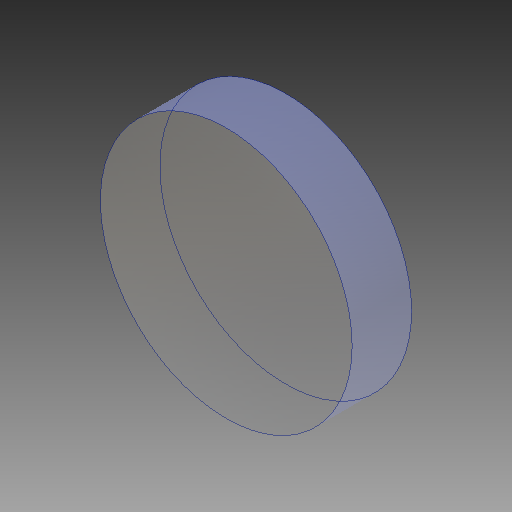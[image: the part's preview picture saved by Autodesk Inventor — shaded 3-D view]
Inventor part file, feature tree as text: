
AUTODESK INVENTOR PART (.ipt)
format: ipt  version: 2017 SP1 (Build 210196100, 196)  size: 107,008 bytes
history: native  units: mm
features: extrude x1, sketch x1
ambient origin geometry x8: Origin, YZ Plane, XZ Plane, XY Plane, X Axis, Y Axis, Z Axis, Center Point
bodies: Solid1 (feature_tree)
feature tree (2):
  extrude  "Extrusion1"  Depth=12.0mm TaperAngle=0.0deg
  sketch  "Sketch1"  dims[d0=50.8mm d1=12.0mm d2=0.0mm]
